# Revit family: RN 62041 Vanne papillon BOAX-SF
name_source: partatom
category: Rohrzubehör
units: mm (PartAtom-declared; Revit-internal decimal feet)

## family parameters
Arbeitsebenenbasiert = Nein
Beim Laden mit Abzugskörper schneiden = Nein
Bemaßung runder Anschluss = Durchmesser verwenden
Gemeinsam genutzt = Nein
Immer vertikal = Ja
Teiletyp = Ventil - Zerlegung in

## types (12) — shared parameters
1.010.00.2 Blattnummer der Richtlinie = 17
1.010.00.3 Ausgabedatum (Monat) der Richtlinie = 201601
1.010.00.4 Herstellername = R. Nussbaum AG
1.010.00.5 Revisionsdatum der Datei = 20190528
1.010.00.6 Webadresse des Herstellers = http://www.nussbaum.ch
1.100.00.3 Sortiernummer für Anzeigereihenfolge = 1
1.100.00.4 Produktbezeichnung = Absperrarmaturen
1.960/3L.00.8 Link (URL) = https://www.nussbaum.ch
17.700.00.4 Armaturentyp = 1
17.700.00.7 Maximale Betriebstemperatur TB [°C] = 90
17.700.00.8 Maximaler Betriebsdruck (Arbeitsdruck) ps [1.0 · 105 Pa] = 16
Connector Visibility = Nein
EnclosingSpace Visibility = Nein
Hersteller = R. Nussbauzm AG
URL = https://www.nussbaum.ch

## per-type parameters (varying)
- DN 40 1: 1.800.00.3 TGA-Nummer=00102200000000000000000000000400600000000000000001???00000; 1.810.00.3 Hersteller-Bestellnummer=62041.25; 1.810.00.4 DATANORM-Nummer=62041.25; 1.810.00.5 StLB-Nummer=723.175; 1.810.00.6 GTIN-Nummer=7612945044624; 17.700.00.30 Produktbeschreibung=62041.25, Absperrklappe BOAX-S, mit Handrad, DN=40; 17.700.00.5 Nennweite DN=40; 17.700.00.6 kvs-Wert [m3/h]=80; CONNECTOR0_DIAMETER_dX_0r=40 mm; CONNECTOR0_dX_00=17 mm; CONNECTOR0_dX_01=17 mm; CONNECTOR0_ref_dX=17 mm; CONNECTOR1_DIAMETER_dX_0r=40 mm; CONNECTOR1_dX_00=17 mm; CONNECTOR1_dX_01=17 mm; CONNECTOR1_ref_dX=17 mm; CONNECTOR2_DIAMETER_dZ_0r=20 mm; CONNECTOR2_dZ_00=122 mm; CONNECTOR2_dZ_01=123 mm; CONNECTOR2_ref_dZ=123 mm; Modell=62041.25; R. Nussbaum AG 62041.05 de Visibility=Nein; R. Nussbaum AG 62041.06 de Visibility=Nein; R. Nussbaum AG 62041.07 de Visibility=Nein; R. Nussbaum AG 62041.08 de Visibility=Nein; R. Nussbaum AG 62041.09 de Visibility=Nein; R. Nussbaum AG 62041.10 de Visibility=Nein; R. Nussbaum AG 62041.11 de Visibility=Nein; R. Nussbaum AG 62041.12 de Visibility=Nein; R. Nussbaum AG 62041.25 de Visibility=Ja; R. Nussbaum AG 62041.30 de Visibility=Nein; R. Nussbaum AG 62041.31 de Visibility=Nein; R. Nussbaum AG 62041.32 de Visibility=Nein; Typenkommentare=Vanne papillon BOAX-SDN 40 1
- DN 125: 1.800.00.3 TGA-Nummer=0010220000000000000000000000040060000000000000000600000000; 1.810.00.3 Hersteller-Bestellnummer=62041.3; 1.810.00.4 DATANORM-Nummer=62041.3; 1.810.00.5 StLB-Nummer=723.182; 1.810.00.6 GTIN-Nummer=7612945044679; 17.700.00.30 Produktbeschreibung=62041.30, Absperrklappe BOAX-S, mit Handrad, DN=125; 17.700.00.5 Nennweite DN=125; 17.700.00.6 kvs-Wert [m3/h]=1200; CONNECTOR0_DIAMETER_dX_0r=125 mm; CONNECTOR0_dX_00=29 mm; CONNECTOR0_dX_01=28 mm  [stored 0.0918635 ft]; CONNECTOR0_ref_dX=28 mm  [stored 0.0918635 ft]; CONNECTOR1_DIAMETER_dX_0r=125 mm; CONNECTOR1_dX_00=28 mm  [stored 0.0918635 ft]; CONNECTOR1_dX_01=29 mm; CONNECTOR1_ref_dX=29 mm; CONNECTOR2_DIAMETER_dZ_0r=43 mm  [stored 0.141076 ft]; CONNECTOR2_dZ_00=201 mm; CONNECTOR2_dZ_01=202 mm; CONNECTOR2_ref_dZ=202 mm; Modell=62041.3; R. Nussbaum AG 62041.05 de Visibility=Nein; R. Nussbaum AG 62041.06 de Visibility=Nein; R. Nussbaum AG 62041.07 de Visibility=Nein; R. Nussbaum AG 62041.08 de Visibility=Nein; R. Nussbaum AG 62041.09 de Visibility=Nein; R. Nussbaum AG 62041.10 de Visibility=Nein; R. Nussbaum AG 62041.11 de Visibility=Nein; R. Nussbaum AG 62041.12 de Visibility=Nein; R. Nussbaum AG 62041.25 de Visibility=Nein; R. Nussbaum AG 62041.30 de Visibility=Ja; R. Nussbaum AG 62041.31 de Visibility=Nein; R. Nussbaum AG 62041.32 de Visibility=Nein; Typenkommentare=Vanne papillon BOAX-SDN 125
- DN 150: 1.800.00.3 TGA-Nummer=0010220000000000000000000000040060000000000000000700000000; 1.810.00.3 Hersteller-Bestellnummer=62041.31; 1.810.00.4 DATANORM-Nummer=62041.31; 1.810.00.5 StLB-Nummer=723.183; 1.810.00.6 GTIN-Nummer=7612945728548; 17.700.00.30 Produktbeschreibung=62041.31, Absperrklappe BOAX-S, mit Handrad, DN=150; 17.700.00.5 Nennweite DN=150; 17.700.00.6 kvs-Wert [m3/h]=1600; CONNECTOR0_DIAMETER_dX_0r=150 mm; CONNECTOR0_dX_00=29 mm; CONNECTOR0_dX_01=28 mm  [stored 0.0918635 ft]; CONNECTOR0_ref_dX=29 mm; CONNECTOR1_DIAMETER_dX_0r=150 mm; CONNECTOR1_dX_00=28 mm  [stored 0.0918635 ft]; CONNECTOR1_dX_01=29 mm; CONNECTOR1_ref_dX=29 mm; CONNECTOR2_DIAMETER_dZ_0r=43 mm  [stored 0.141076 ft]; CONNECTOR2_dZ_00=201 mm; CONNECTOR2_dZ_01=202 mm; CONNECTOR2_ref_dZ=202 mm; Modell=62041.31; R. Nussbaum AG 62041.05 de Visibility=Nein; R. Nussbaum AG 62041.06 de Visibility=Nein; R. Nussbaum AG 62041.07 de Visibility=Nein; R. Nussbaum AG 62041.08 de Visibility=Nein; R. Nussbaum AG 62041.09 de Visibility=Nein; R. Nussbaum AG 62041.10 de Visibility=Nein; R. Nussbaum AG 62041.11 de Visibility=Nein; R. Nussbaum AG 62041.12 de Visibility=Nein; R. Nussbaum AG 62041.25 de Visibility=Nein; R. Nussbaum AG 62041.30 de Visibility=Nein; R. Nussbaum AG 62041.31 de Visibility=Ja; R. Nussbaum AG 62041.32 de Visibility=Nein; Typenkommentare=Vanne papillon BOAX-SDN 150
- DN 200 1: 1.800.00.3 TGA-Nummer=0010220000000000000000000000040060000000000000000800000000; 1.810.00.3 Hersteller-Bestellnummer=62041.32; 1.810.00.4 DATANORM-Nummer=62041.32; 1.810.00.5 StLB-Nummer=723.184; 1.810.00.6 GTIN-Nummer=7612945728555; 17.700.00.30 Produktbeschreibung=62041.32, Absperrklappe BOAX-S, mit Handrad, DN=200; 17.700.00.5 Nennweite DN=200; 17.700.00.6 kvs-Wert [m3/h]=3200; CONNECTOR0_DIAMETER_dX_0r=200 mm; CONNECTOR0_dX_00=31 mm  [stored 0.101706 ft]; CONNECTOR0_dX_01=30 mm  [stored 0.0984252 ft]; CONNECTOR0_ref_dX=31 mm  [stored 0.101706 ft]; CONNECTOR1_DIAMETER_dX_0r=200 mm; CONNECTOR1_dX_00=30 mm  [stored 0.0984252 ft]; CONNECTOR1_dX_01=31 mm  [stored 0.101706 ft]; CONNECTOR1_ref_dX=31 mm  [stored 0.101706 ft]; CONNECTOR2_DIAMETER_dZ_0r=43 mm  [stored 0.141076 ft]; CONNECTOR2_dZ_00=201 mm; CONNECTOR2_dZ_01=202 mm; CONNECTOR2_ref_dZ=202 mm; Modell=62041.32; R. Nussbaum AG 62041.05 de Visibility=Nein; R. Nussbaum AG 62041.06 de Visibility=Nein; R. Nussbaum AG 62041.07 de Visibility=Nein; R. Nussbaum AG 62041.08 de Visibility=Nein; R. Nussbaum AG 62041.09 de Visibility=Nein; R. Nussbaum AG 62041.10 de Visibility=Nein; R. Nussbaum AG 62041.11 de Visibility=Nein; R. Nussbaum AG 62041.12 de Visibility=Nein; R. Nussbaum AG 62041.25 de Visibility=Nein; R. Nussbaum AG 62041.30 de Visibility=Nein; R. Nussbaum AG 62041.31 de Visibility=Nein; R. Nussbaum AG 62041.32 de Visibility=Ja; Typenkommentare=Vanne papillon BOAX-SDN 200 1
- DN 40: 1.800.00.3 TGA-Nummer=00109000000000000000000000000400600000000000000001???00000; 1.810.00.3 Hersteller-Bestellnummer=62041.05; 1.810.00.4 DATANORM-Nummer=62041.05; 1.810.00.5 StLB-Nummer=723.175; 1.810.00.6 GTIN-Nummer=7612945819697; 17.700.00.30 Produktbeschreibung=62041.05, Absperrklappe BOAX-SF, mit Handrad, DN=40; 17.700.00.5 Nennweite DN=40; 17.700.00.6 kvs-Wert [m3/h]=80; CONNECTOR0_DIAMETER_dX_0r=40 mm; CONNECTOR0_dX_00=17 mm; CONNECTOR0_dX_01=17 mm; CONNECTOR0_ref_dX=17 mm; CONNECTOR1_DIAMETER_dX_0r=40 mm; CONNECTOR1_dX_00=17 mm; CONNECTOR1_dX_01=17 mm; CONNECTOR1_ref_dX=17 mm; CONNECTOR2_DIAMETER_dZ_0r=43 mm  [stored 0.141076 ft]; CONNECTOR2_dZ_00=201 mm; CONNECTOR2_dZ_01=202 mm; CONNECTOR2_ref_dZ=202 mm; Modell=62041.05; R. Nussbaum AG 62041.05 de Visibility=Ja; R. Nussbaum AG 62041.06 de Visibility=Nein; R. Nussbaum AG 62041.07 de Visibility=Nein; R. Nussbaum AG 62041.08 de Visibility=Nein; R. Nussbaum AG 62041.09 de Visibility=Nein; R. Nussbaum AG 62041.10 de Visibility=Nein; R. Nussbaum AG 62041.11 de Visibility=Nein; R. Nussbaum AG 62041.12 de Visibility=Nein; R. Nussbaum AG 62041.25 de Visibility=Nein; R. Nussbaum AG 62041.30 de Visibility=Nein; R. Nussbaum AG 62041.31 de Visibility=Nein; R. Nussbaum AG 62041.32 de Visibility=Nein; Typenkommentare=Vanne papillon BOAX-SFDN 40
- DN 50: 1.800.00.3 TGA-Nummer=00109000000000000000000000000400600000000000000002???00000; 1.810.00.3 Hersteller-Bestellnummer=62041.06; 1.810.00.4 DATANORM-Nummer=62041.06; 1.810.00.5 StLB-Nummer=723.176; 1.810.00.6 GTIN-Nummer=7612945819703; 17.700.00.30 Produktbeschreibung=62041.06, Absperrklappe BOAX-SF, mit Handrad, DN=50; 17.700.00.5 Nennweite DN=50; 17.700.00.6 kvs-Wert [m3/h]=130; CONNECTOR0_DIAMETER_dX_0r=50 mm; CONNECTOR0_dX_00=22 mm  [stored 0.0721785 ft]; CONNECTOR0_dX_01=22 mm  [stored 0.0721785 ft]; CONNECTOR0_ref_dX=22 mm  [stored 0.0721785 ft]; CONNECTOR1_DIAMETER_dX_0r=50 mm; CONNECTOR1_dX_00=22 mm  [stored 0.0721785 ft]; CONNECTOR1_dX_01=22 mm  [stored 0.0721785 ft]; CONNECTOR1_ref_dX=22 mm  [stored 0.0721785 ft]; CONNECTOR2_DIAMETER_dZ_0r=43 mm  [stored 0.141076 ft]; CONNECTOR2_dZ_00=201 mm; CONNECTOR2_dZ_01=202 mm; CONNECTOR2_ref_dZ=202 mm; Modell=62041.06; R. Nussbaum AG 62041.05 de Visibility=Nein; R. Nussbaum AG 62041.06 de Visibility=Ja; R. Nussbaum AG 62041.07 de Visibility=Nein; R. Nussbaum AG 62041.08 de Visibility=Nein; R. Nussbaum AG 62041.09 de Visibility=Nein; R. Nussbaum AG 62041.10 de Visibility=Nein; R. Nussbaum AG 62041.11 de Visibility=Nein; R. Nussbaum AG 62041.12 de Visibility=Nein; R. Nussbaum AG 62041.25 de Visibility=Nein; R. Nussbaum AG 62041.30 de Visibility=Nein; R. Nussbaum AG 62041.31 de Visibility=Nein; R. Nussbaum AG 62041.32 de Visibility=Nein; Typenkommentare=Vanne papillon BOAX-SFDN 50
- DN 65: 1.800.00.3 TGA-Nummer=00109000000000000000000000000400600000000000000003???00000; 1.810.00.3 Hersteller-Bestellnummer=62041.07; 1.810.00.4 DATANORM-Nummer=62041.07; 1.810.00.5 StLB-Nummer=723.177; 1.810.00.6 GTIN-Nummer=7612945819710; 17.700.00.30 Produktbeschreibung=62041.07, Absperrklappe BOAX-SF, mit Handrad, DN=65; 17.700.00.5 Nennweite DN=65; 17.700.00.6 kvs-Wert [m3/h]=275; CONNECTOR0_DIAMETER_dX_0r=65 mm; CONNECTOR0_dX_00=24 mm; CONNECTOR0_dX_01=23 mm  [stored 0.0754593 ft]; CONNECTOR0_ref_dX=24 mm; CONNECTOR1_DIAMETER_dX_0r=65 mm; CONNECTOR1_dX_00=23 mm  [stored 0.0754593 ft]; CONNECTOR1_dX_01=24 mm; CONNECTOR1_ref_dX=24 mm; CONNECTOR2_DIAMETER_dZ_0r=43 mm  [stored 0.141076 ft]; CONNECTOR2_dZ_00=201 mm; CONNECTOR2_dZ_01=202 mm; CONNECTOR2_ref_dZ=202 mm; Modell=62041.07; R. Nussbaum AG 62041.05 de Visibility=Nein; R. Nussbaum AG 62041.06 de Visibility=Nein; R. Nussbaum AG 62041.07 de Visibility=Ja; R. Nussbaum AG 62041.08 de Visibility=Nein; R. Nussbaum AG 62041.09 de Visibility=Nein; R. Nussbaum AG 62041.10 de Visibility=Nein; R. Nussbaum AG 62041.11 de Visibility=Nein; R. Nussbaum AG 62041.12 de Visibility=Nein; R. Nussbaum AG 62041.25 de Visibility=Nein; R. Nussbaum AG 62041.30 de Visibility=Nein; R. Nussbaum AG 62041.31 de Visibility=Nein; R. Nussbaum AG 62041.32 de Visibility=Nein; Typenkommentare=Vanne papillon BOAX-SFDN 65
- DN 80: 1.800.00.3 TGA-Nummer=00109000000000000000000000000400600000000000000004???00000; 1.810.00.3 Hersteller-Bestellnummer=62041.08; 1.810.00.4 DATANORM-Nummer=62041.08; 1.810.00.5 StLB-Nummer=723.178; 1.810.00.6 GTIN-Nummer=7612945819727; 17.700.00.30 Produktbeschreibung=62041.08, Absperrklappe BOAX-SF, mit Handrad, DN=80; 17.700.00.5 Nennweite DN=80; 17.700.00.6 kvs-Wert [m3/h]=410; CONNECTOR0_DIAMETER_dX_0r=80 mm; CONNECTOR0_dX_00=24 mm; CONNECTOR0_dX_01=23 mm  [stored 0.0754593 ft]; CONNECTOR0_ref_dX=24 mm; CONNECTOR1_DIAMETER_dX_0r=80 mm; CONNECTOR1_dX_00=23 mm  [stored 0.0754593 ft]; CONNECTOR1_dX_01=24 mm; CONNECTOR1_ref_dX=24 mm; CONNECTOR2_DIAMETER_dZ_0r=43 mm  [stored 0.141076 ft]; CONNECTOR2_dZ_00=201 mm; CONNECTOR2_dZ_01=202 mm; CONNECTOR2_ref_dZ=202 mm; Modell=62041.08; R. Nussbaum AG 62041.05 de Visibility=Nein; R. Nussbaum AG 62041.06 de Visibility=Nein; R. Nussbaum AG 62041.07 de Visibility=Nein; R. Nussbaum AG 62041.08 de Visibility=Ja; R. Nussbaum AG 62041.09 de Visibility=Nein; R. Nussbaum AG 62041.10 de Visibility=Nein; R. Nussbaum AG 62041.11 de Visibility=Nein; R. Nussbaum AG 62041.12 de Visibility=Nein; R. Nussbaum AG 62041.25 de Visibility=Nein; R. Nussbaum AG 62041.30 de Visibility=Nein; R. Nussbaum AG 62041.31 de Visibility=Nein; R. Nussbaum AG 62041.32 de Visibility=Nein; Typenkommentare=Vanne papillon BOAX-SFDN 80
- DN 100: 1.800.00.3 TGA-Nummer=00109000000000000000000000000400600000000000000005???00000; 1.810.00.3 Hersteller-Bestellnummer=62041.09; 1.810.00.4 DATANORM-Nummer=62041.09; 1.810.00.5 StLB-Nummer=723.181; 1.810.00.6 GTIN-Nummer=7612945819734; 17.700.00.30 Produktbeschreibung=62041.09, Absperrklappe BOAX-SF, mit Handrad, DN=100; 17.700.00.5 Nennweite DN=100; 17.700.00.6 kvs-Wert [m3/h]=650; CONNECTOR0_DIAMETER_dX_0r=100 mm  [stored 0.328084 ft]; CONNECTOR0_dX_00=27 mm; CONNECTOR0_dX_01=26 mm; CONNECTOR0_ref_dX=27 mm; CONNECTOR1_DIAMETER_dX_0r=100 mm  [stored 0.328084 ft]; CONNECTOR1_dX_00=26 mm; CONNECTOR1_dX_01=27 mm; CONNECTOR1_ref_dX=27 mm; CONNECTOR2_DIAMETER_dZ_0r=43 mm  [stored 0.141076 ft]; CONNECTOR2_dZ_00=201 mm; CONNECTOR2_dZ_01=202 mm; CONNECTOR2_ref_dZ=202 mm; Modell=62041.09; R. Nussbaum AG 62041.05 de Visibility=Nein; R. Nussbaum AG 62041.06 de Visibility=Nein; R. Nussbaum AG 62041.07 de Visibility=Nein; R. Nussbaum AG 62041.08 de Visibility=Nein; R. Nussbaum AG 62041.09 de Visibility=Ja; R. Nussbaum AG 62041.10 de Visibility=Nein; R. Nussbaum AG 62041.11 de Visibility=Nein; R. Nussbaum AG 62041.12 de Visibility=Nein; R. Nussbaum AG 62041.25 de Visibility=Nein; R. Nussbaum AG 62041.30 de Visibility=Nein; R. Nussbaum AG 62041.31 de Visibility=Nein; R. Nussbaum AG 62041.32 de Visibility=Nein; Typenkommentare=Vanne papillon BOAX-SFDN 100
- DN 125 1: 1.800.00.3 TGA-Nummer=0010900000000000000000000000040060000000000000000600000000; 1.810.00.3 Hersteller-Bestellnummer=62041.1; 1.810.00.4 DATANORM-Nummer=62041.1; 1.810.00.5 StLB-Nummer=723.182; 1.810.00.6 GTIN-Nummer=7612945819741; 17.700.00.30 Produktbeschreibung=62041.10, Absperrklappe BOAX-SF, mit Handrad, DN=125; 17.700.00.5 Nennweite DN=125; 17.700.00.6 kvs-Wert [m3/h]=1200; CONNECTOR0_DIAMETER_dX_0r=125 mm; CONNECTOR0_dX_00=29 mm; CONNECTOR0_dX_01=28 mm  [stored 0.0918635 ft]; CONNECTOR0_ref_dX=29 mm; CONNECTOR1_DIAMETER_dX_0r=125 mm; CONNECTOR1_dX_00=28 mm  [stored 0.0918635 ft]; CONNECTOR1_dX_01=29 mm; CONNECTOR1_ref_dX=29 mm; CONNECTOR2_DIAMETER_dZ_0r=43 mm  [stored 0.141076 ft]; CONNECTOR2_dZ_00=201 mm; CONNECTOR2_dZ_01=202 mm; CONNECTOR2_ref_dZ=202 mm; Modell=62041.1; R. Nussbaum AG 62041.05 de Visibility=Nein; R. Nussbaum AG 62041.06 de Visibility=Nein; R. Nussbaum AG 62041.07 de Visibility=Nein; R. Nussbaum AG 62041.08 de Visibility=Nein; R. Nussbaum AG 62041.09 de Visibility=Nein; R. Nussbaum AG 62041.10 de Visibility=Ja; R. Nussbaum AG 62041.11 de Visibility=Nein; R. Nussbaum AG 62041.12 de Visibility=Nein; R. Nussbaum AG 62041.25 de Visibility=Nein; R. Nussbaum AG 62041.30 de Visibility=Nein; R. Nussbaum AG 62041.31 de Visibility=Nein; R. Nussbaum AG 62041.32 de Visibility=Nein; Typenkommentare=Vanne papillon BOAX-SFDN 125 1
- DN 150 1: 1.800.00.3 TGA-Nummer=0010900000000000000000000000040060000000000000000700000000; 1.810.00.3 Hersteller-Bestellnummer=62041.11; 1.810.00.4 DATANORM-Nummer=62041.11; 1.810.00.5 StLB-Nummer=723.183; 1.810.00.6 GTIN-Nummer=7612945819758; 17.700.00.30 Produktbeschreibung=62041.11, Absperrklappe BOAX-SF, mit Handrad, DN=150; 17.700.00.5 Nennweite DN=150; 17.700.00.6 kvs-Wert [m3/h]=1600; CONNECTOR0_DIAMETER_dX_0r=150 mm; CONNECTOR0_dX_00=29 mm; CONNECTOR0_dX_01=28 mm  [stored 0.0918635 ft]; CONNECTOR0_ref_dX=29 mm; CONNECTOR1_DIAMETER_dX_0r=150 mm; CONNECTOR1_dX_00=28 mm  [stored 0.0918635 ft]; CONNECTOR1_dX_01=29 mm; CONNECTOR1_ref_dX=29 mm; CONNECTOR2_DIAMETER_dZ_0r=43 mm  [stored 0.141076 ft]; CONNECTOR2_dZ_00=201 mm; CONNECTOR2_dZ_01=202 mm; CONNECTOR2_ref_dZ=202 mm; Modell=62041.11; R. Nussbaum AG 62041.05 de Visibility=Nein; R. Nussbaum AG 62041.06 de Visibility=Nein; R. Nussbaum AG 62041.07 de Visibility=Nein; R. Nussbaum AG 62041.08 de Visibility=Nein; R. Nussbaum AG 62041.09 de Visibility=Nein; R. Nussbaum AG 62041.10 de Visibility=Nein; R. Nussbaum AG 62041.11 de Visibility=Ja; R. Nussbaum AG 62041.12 de Visibility=Nein; R. Nussbaum AG 62041.25 de Visibility=Nein; R. Nussbaum AG 62041.30 de Visibility=Nein; R. Nussbaum AG 62041.31 de Visibility=Nein; R. Nussbaum AG 62041.32 de Visibility=Nein; Typenkommentare=Vanne papillon BOAX-SFDN 150 1
- DN 200: 1.800.00.3 TGA-Nummer=0010900000000000000000000000040060000000000000000800000000; 1.810.00.3 Hersteller-Bestellnummer=62041.12; 1.810.00.4 DATANORM-Nummer=62041.12; 1.810.00.5 StLB-Nummer=723.184; 1.810.00.6 GTIN-Nummer=7612945819765; 17.700.00.30 Produktbeschreibung=62041.12, Absperrklappe BOAX-SF, mit Handrad, DN=200; 17.700.00.5 Nennweite DN=200; 17.700.00.6 kvs-Wert [m3/h]=3200; CONNECTOR0_DIAMETER_dX_0r=200 mm; CONNECTOR0_dX_00=31 mm  [stored 0.101706 ft]; CONNECTOR0_dX_01=30 mm  [stored 0.0984252 ft]; CONNECTOR0_ref_dX=31 mm  [stored 0.101706 ft]; CONNECTOR1_DIAMETER_dX_0r=200 mm; CONNECTOR1_dX_00=30 mm  [stored 0.0984252 ft]; CONNECTOR1_dX_01=31 mm  [stored 0.101706 ft]; CONNECTOR1_ref_dX=31 mm  [stored 0.101706 ft]; CONNECTOR2_DIAMETER_dZ_0r=43 mm  [stored 0.141076 ft]; CONNECTOR2_dZ_00=201 mm; CONNECTOR2_dZ_01=202 mm; CONNECTOR2_ref_dZ=202 mm; Modell=62041.12; R. Nussbaum AG 62041.05 de Visibility=Nein; R. Nussbaum AG 62041.06 de Visibility=Nein; R. Nussbaum AG 62041.07 de Visibility=Nein; R. Nussbaum AG 62041.08 de Visibility=Nein; R. Nussbaum AG 62041.09 de Visibility=Nein; R. Nussbaum AG 62041.10 de Visibility=Nein; R. Nussbaum AG 62041.11 de Visibility=Nein; R. Nussbaum AG 62041.12 de Visibility=Ja; R. Nussbaum AG 62041.25 de Visibility=Nein; R. Nussbaum AG 62041.30 de Visibility=Nein; R. Nussbaum AG 62041.31 de Visibility=Nein; R. Nussbaum AG 62041.32 de Visibility=Nein; Typenkommentare=Vanne papillon BOAX-SFDN 200

note: [stored X ft] marks values corroborated as IEEE doubles in the binary element streams (Revit-internal decimal feet)

## geometry (parser evidence)
native form markers: Sweep x3
no freeform markers — native parametric forms only
